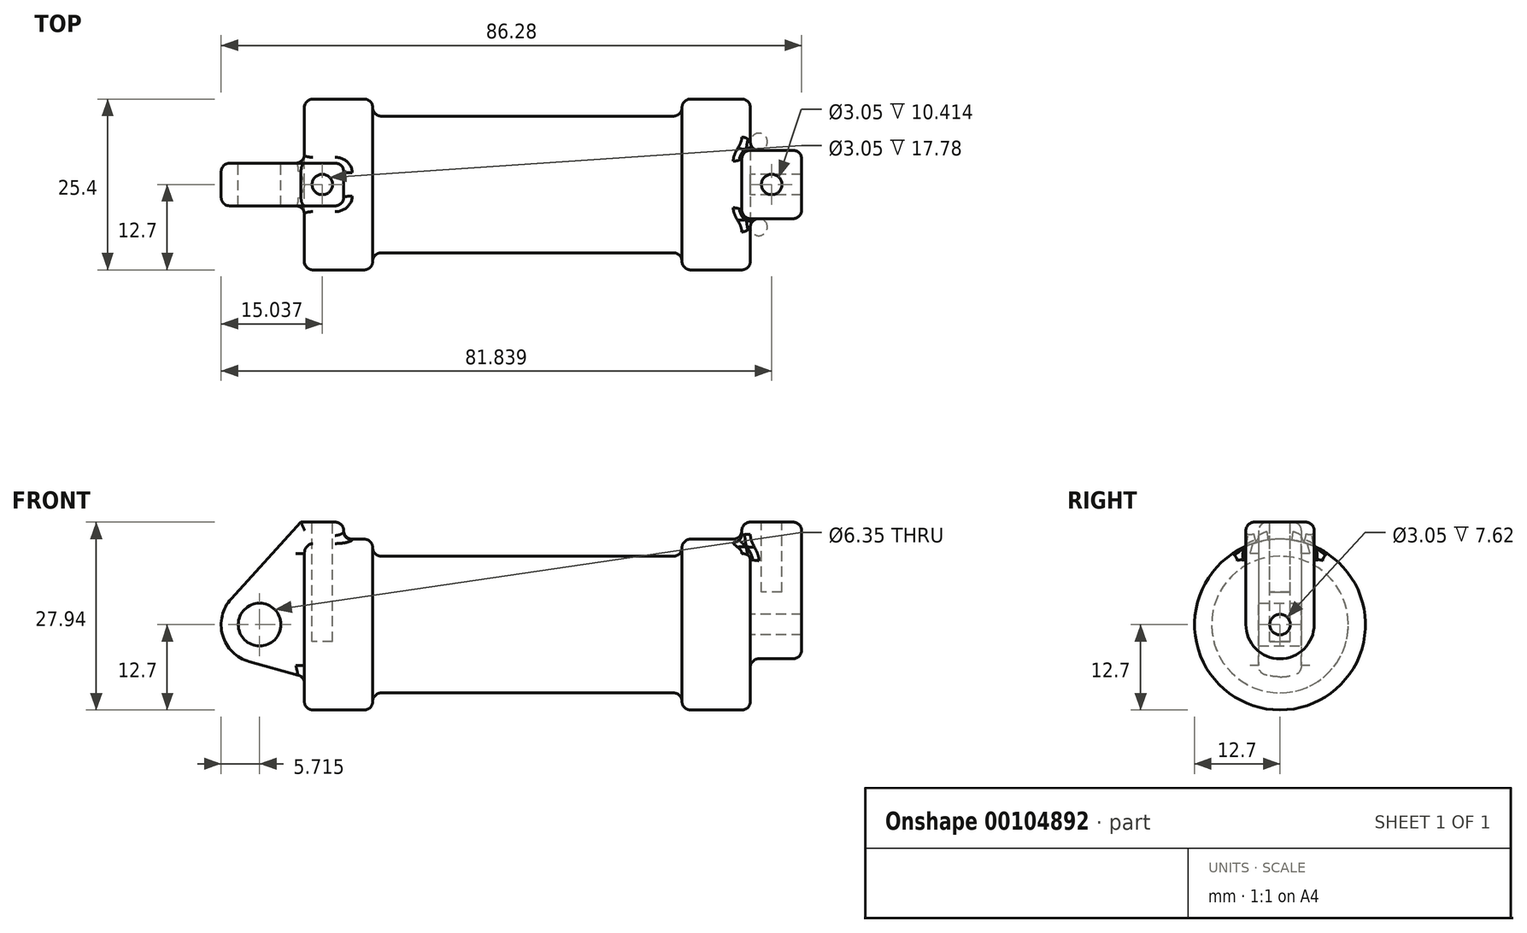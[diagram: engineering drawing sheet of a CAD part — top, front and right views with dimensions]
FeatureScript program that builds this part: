
annotation { "Feature Type Name" : "Feature", "Feature Type Description" : "" }
export const myFeature = defineFeature(function(context is Context, id is Id, definition is map)
    precondition{}
    {
        {
            var Q0;
            Q0=qCreatedBy(makeId("Front.planeOp"),FACE);
            var sketch = newSketch(context, id + "F0", { "sketchPlane" : qUnion([Q0])});
            skLineSegment(sketch, "E0", {"start": v(0, 0) * mm, "end": v(0, 12.7) * mm});
            skLineSegment(sketch, "E1", {"start": v(0, 12.7) * mm, "end": v(10.16, 12.7) * mm});
            skLineSegment(sketch, "E2", {"start": v(10.16, 12.7) * mm, "end": v(10.16, 10.16) * mm});
            skLineSegment(sketch, "E3", {"start": v(10.16, 10.16) * mm, "end": v(56.13, 10.16) * mm});
            skLineSegment(sketch, "E4", {"start": v(56.13, 10.16) * mm, "end": v(56.13, 12.7) * mm});
            skLineSegment(sketch, "E5", {"start": v(56.13, 12.7) * mm, "end": v(66.3, 12.7) * mm});
            skLineSegment(sketch, "E6", {"start": v(66.3, 12.7) * mm, "end": v(66.3, 0) * mm});
            skLineSegment(sketch, "E7", {"start": v(66.3, 0) * mm, "end": v(0, 0) * mm});
            skLineSegment(sketch, "E8", {"start": v(5.84, 15.24) * mm, "end": v(-0.5, 15.24) * mm});
            skLineSegment(sketch, "E9", {"start": v(-0.5, 15.24) * mm, "end": v(-10.88, 3.85) * mm});
            skLineSegment(sketch, "E10", {"start": v(0, 0) * mm, "end": v(-6.65, 0) * mm});
            skCircle(sketch, "E11", {"center": v(-6.65, 0) * mm, "radius": 5.72 * mm});
            skCircle(sketch, "E12", {"center": v(-6.65, 0) * mm, "radius": 3.18 * mm});
            skLineSegment(sketch, "E13", {"start": v(5.84, 15.24) * mm, "end": v(5.84, -9.4) * mm});
            skLineSegment(sketch, "E14", {"start": v(5.84, -9.4) * mm, "end": v(-8.18, -5.5) * mm});
            skSolve(sketch);
        }
        {
            var Q0;
            {var subQ0=sQuery(id+"F0.wireOp",EDGE,"E2");Q0=makeQuery(id+"F0.imprint","IMPRINT",FACE,{"disambiguationData":[TD([[makeQuery(id+"F0.imprint","IMPRINT",EDGE,{"derivedFrom":subQ0}),-1.0]])]});}
            var Q1;
            {var subQ0=sQuery(id+"F0.wireOp",EDGE,"E0");Q1=makeQuery(id+"F0.imprint","IMPRINT",FACE,{"disambiguationData":[TD([[makeQuery(id+"F0.imprint","IMPRINT",EDGE,{"derivedFrom":subQ0}),-1.0]])]});}
            var Q2;
            Q2=sQuery(id+"F0.wireOp",EDGE,"E7");
            revolve(context, id + "F1", {"entities" : qUnion([Q0, Q1]), "axis" : qUnion([Q2]), "revolveType" : RevolveType.FULL});
        }
        {
            var Q0;
            {var subQ0=sQuery(id+"F0.wireOp",EDGE,"E0");Q0=makeQuery(id+"F0.imprint","IMPRINT",FACE,{"disambiguationData":[TD([[makeQuery(id+"F0.imprint","IMPRINT",EDGE,{"derivedFrom":subQ0}),-1.0]])]});}
            var Q1;
            {var subQ3=sQuery(id+"F0.wireOp",EDGE,"E0");Q1=makeQuery(id+"F0.imprint","IMPRINT",FACE,{"disambiguationData":[TD([[makeQuery(id+"F0.imprint","IMPRINT",EDGE,{"derivedFrom":subQ3}),1.0]])]});}
            var Q2;
            {var subQ4=sQuery(id+"F0.wireOp",EDGE,"E12");Q2=makeQuery(id+"F0.imprint","IMPRINT",FACE,{"disambiguationData":[TD([[makeQuery(id+"F0.imprint","IMPRINT",EDGE,{"derivedFrom":subQ4}),-1.0]])]});}
            var Q3;
            {var subQ0=sQuery(id+"F0.wireOp",EDGE,"E14");Q3=makeQuery(id+"F0.imprint","IMPRINT",FACE,{"disambiguationData":[TD([[makeQuery(id+"F0.imprint","IMPRINT",EDGE,{"derivedFrom":subQ0}),-1.0]])]});}
            extrude(context, id + "F2", {"entities" : qUnion([Q0, Q1, Q2, Q3]), "operationType" : NewBodyOperationType.ADD, "depth" : 3.17 * mm, "hasSecondDirection" : true, "secondDirectionOppositeDirection" : true, "secondDirectionDepth" : 3.17 * mm});
        }
        {
            var Q0;
            Q0=makeQuery(id+"F1.opRevolve","SWEPT_FACE",FACE,{"disambiguationData":[OSD([sQuery(id+"F0.wireOp",EDGE,"E6")])]});
            cPlane(context, id + "F3", {"entities" : qUnion([Q0]), "cplaneType" : CPlaneType.OFFSET, "offset" : 0 * mm, "width" : 152.4 * mm, "height" : 152.4 * mm});
        }
        {
            var Q0;
            Q0=qCreatedBy(id+"F3.planeOp",FACE);
            var sketch = newSketch(context, id + "F4", { "sketchPlane" : qUnion([Q0])});
            skCircle(sketch, "E15", {"center": v(0, 0) * mm, "radius": 5.08 * mm});
            skCircle(sketch, "E16", {"center": v(0, 0) * mm, "radius": 1.52 * mm});
            skLineSegment(sketch, "E17", {"start": v(-5.08, 15.24) * mm, "end": v(5.08, 15.24) * mm});
            skLineSegment(sketch, "E18", {"start": v(5.08, 15.24) * mm, "end": v(5.08, 0) * mm});
            skLineSegment(sketch, "E19", {"start": v(-5.08, 15.24) * mm, "end": v(-5.08, 0) * mm});
            skSolve(sketch);
        }
        {
            var Q0;
            Q0 = qSketchRegion(id + "F4", true);
            extrude(context, id + "F5", {"entities" : qUnion([Q0]), "operationType" : NewBodyOperationType.ADD, "depth" : 7.62 * mm, "hasSecondDirection" : true, "secondDirectionOppositeDirection" : true, "secondDirectionDepth" : 1.27 * mm});
        }
        {
            var Q0;
            Q0=makeQuery(id+"F5.opExtrude","SWEPT_FACE",FACE,{"disambiguationData":[OSD([sQuery(id+"F4.wireOp",EDGE,"E17")])]});
            cPlane(context, id + "F6", {"entities" : qUnion([Q0]), "cplaneType" : CPlaneType.OFFSET, "offset" : 0 * mm, "width" : 152.4 * mm, "height" : 152.4 * mm});
        }
        {
            var Q0;
            Q0=qCreatedBy(id+"F6.planeOp",FACE);
            var sketch = newSketch(context, id + "F7", { "sketchPlane" : qUnion([Q0])});
            skCircle(sketch, "E20", {"center": v(69.47, 0) * mm, "radius": 1.52 * mm});
            skLineSegment(sketch, "E21", {"start": v(73.91, 0) * mm, "end": v(65.02, 0) * mm, "construction": true});
            skSolve(sketch);
        }
        {
            var Q0;
            Q0=makeQuery(id+"F7.imprint","IMPRINT",FACE,{"disambiguationData":[TD([[makeQuery(id+"F7.imprint","IMPRINT",EDGE,{"derivedFrom":sQuery(id+"F7.wireOp",EDGE,"E20")}),1.0]])]});
            extrude(context, id + "F8", {"entities" : qUnion([Q0]), "operationType" : NewBodyOperationType.REMOVE, "oppositeDirection" : true, "depth" : 10.4 * mm});
        }
        {
            var Q0;
            Q0=qCreatedBy(id+"F6.planeOp",FACE);
            var sketch = newSketch(context, id + "F9", { "sketchPlane" : qUnion([Q0])});
            skCircle(sketch, "E22", {"center": v(2.67, 0) * mm, "radius": 1.52 * mm});
            skSolve(sketch);
        }
        {
            var Q0;
            Q0 = qSketchRegion(id + "F9", true);
            extrude(context, id + "F10", {"entities" : qUnion([Q0]), "operationType" : NewBodyOperationType.REMOVE, "oppositeDirection" : true, "depth" : 17.78 * mm});
        }
        {
            var Q0;
            Q0=makeQuery(id+"F1.opRevolve","SWEPT_EDGE",EDGE,{"disambiguationData":[OSD([sQuery(id+"F0.wireOp",EDGE,"E1"),sQuery(id+"F0.wireOp",EDGE,"E2")])]});
            var Q1;
            Q1=makeQuery(id+"F1.opRevolve","SWEPT_EDGE",EDGE,{"disambiguationData":[OSD([sQuery(id+"F0.wireOp",EDGE,"E2"),sQuery(id+"F0.wireOp",EDGE,"E3")])]});
            var Q2;
            Q2=makeQuery(id+"F2.boolean.opBoolean","INTERSECT",EDGE,{"derivedFrom":[makeQuery(id+"F1.opRevolve","SWEPT_FACE",FACE,{"disambiguationData":[OSD([sQuery(id+"F0.wireOp",EDGE,"E1")])]}),makeQuery(id+"F2.opExtrude","CAP_FACE",FACE,{"disambiguationData":[OSD([sQuery(id+"F0.wireOp",EDGE,"E8"),sQuery(id+"F0.wireOp",EDGE,"E9"),sQuery(id+"F0.wireOp",EDGE,"E11"),sQuery(id+"F0.wireOp",EDGE,"E12"),sQuery(id+"F0.wireOp",EDGE,"E13"),sQuery(id+"F0.wireOp",EDGE,"E14")])],"isStart":false})]});
            var Q3;
            Q3=makeQuery(id+"F2.boolean.opBoolean","INTERSECT",EDGE,{"derivedFrom":[makeQuery(id+"F1.opRevolve","SWEPT_FACE",FACE,{"disambiguationData":[OSD([sQuery(id+"F0.wireOp",EDGE,"E1")])]}),makeQuery(id+"F2.opExtrude","SWEPT_FACE",FACE,{"disambiguationData":[OSD([sQuery(id+"F0.wireOp",EDGE,"E13")])]})]});
            var Q4;
            Q4=makeQuery(id+"F2.opExtrude","SWEPT_EDGE",EDGE,{"disambiguationData":[OSD([sQuery(id+"F0.wireOp",EDGE,"E8"),sQuery(id+"F0.wireOp",EDGE,"E13")])]});
            var Q5;
            Q5=makeQuery(id+"F2.opExtrude","CAP_EDGE",EDGE,{"disambiguationData":[OSD([sQuery(id+"F0.wireOp",EDGE,"E8")])],"isStart":false});
            var Q6;
            Q6=makeQuery(id+"F2.opExtrude","CAP_EDGE",EDGE,{"disambiguationData":[OSD([sQuery(id+"F0.wireOp",EDGE,"E8")])],"isStart":true});
            var Q7;
            Q7=makeQuery(id+"F2.boolean.opBoolean","INTERSECT",EDGE,{"derivedFrom":[makeQuery(id+"F1.opRevolve","SWEPT_FACE",FACE,{"disambiguationData":[OSD([sQuery(id+"F0.wireOp",EDGE,"E1")])]}),makeQuery(id+"F2.opExtrude","CAP_FACE",FACE,{"disambiguationData":[OSD([sQuery(id+"F0.wireOp",EDGE,"E8"),sQuery(id+"F0.wireOp",EDGE,"E9"),sQuery(id+"F0.wireOp",EDGE,"E11"),sQuery(id+"F0.wireOp",EDGE,"E12"),sQuery(id+"F0.wireOp",EDGE,"E13"),sQuery(id+"F0.wireOp",EDGE,"E14")])],"isStart":true})]});
            var Q8;
            Q8=makeQuery(id+"F2.opExtrude","CAP_EDGE",EDGE,{"disambiguationData":[OSD([sQuery(id+"F0.wireOp",EDGE,"E9")])],"isStart":false});
            var Q9;
            Q9=makeQuery(id+"F2.opExtrude","CAP_EDGE",EDGE,{"disambiguationData":[OSD([sQuery(id+"F0.wireOp",EDGE,"E11")])],"isStart":true});
            var Q10;
            Q10=makeQuery(id+"F2.opExtrude","CAP_EDGE",EDGE,{"disambiguationData":[OSD([sQuery(id+"F0.wireOp",EDGE,"E9")])],"isStart":true});
            var Q11;
            Q11=makeQuery(id+"F2.opExtrude","CAP_EDGE",EDGE,{"disambiguationData":[OSD([sQuery(id+"F0.wireOp",EDGE,"E11")])],"isStart":false});
            var Q12;
            Q12=makeQuery(id+"F2.opExtrude","CAP_EDGE",EDGE,{"disambiguationData":[OSD([sQuery(id+"F0.wireOp",EDGE,"E14")])],"isStart":true});
            var Q13;
            Q13=makeQuery(id+"F2.opExtrude","CAP_EDGE",EDGE,{"disambiguationData":[OSD([sQuery(id+"F0.wireOp",EDGE,"E14")])],"isStart":false});
            var Q14;
            Q14=makeQuery(id+"F2.boolean.opBoolean","INTERSECT",EDGE,{"derivedFrom":[makeQuery(id+"F1.opRevolve","SWEPT_FACE",FACE,{"disambiguationData":[OSD([sQuery(id+"F0.wireOp",EDGE,"E0")])]}),makeQuery(id+"F2.opExtrude","CAP_FACE",FACE,{"disambiguationData":[OSD([sQuery(id+"F0.wireOp",EDGE,"E8"),sQuery(id+"F0.wireOp",EDGE,"E9"),sQuery(id+"F0.wireOp",EDGE,"E11"),sQuery(id+"F0.wireOp",EDGE,"E12"),sQuery(id+"F0.wireOp",EDGE,"E13"),sQuery(id+"F0.wireOp",EDGE,"E14")])],"isStart":false})]});
            var Q15;
            Q15=makeQuery(id+"F2.boolean.opBoolean","INTERSECT",EDGE,{"derivedFrom":[makeQuery(id+"F1.opRevolve","SWEPT_FACE",FACE,{"disambiguationData":[OSD([sQuery(id+"F0.wireOp",EDGE,"E0")])]}),makeQuery(id+"F2.opExtrude","CAP_FACE",FACE,{"disambiguationData":[OSD([sQuery(id+"F0.wireOp",EDGE,"E8"),sQuery(id+"F0.wireOp",EDGE,"E9"),sQuery(id+"F0.wireOp",EDGE,"E11"),sQuery(id+"F0.wireOp",EDGE,"E12"),sQuery(id+"F0.wireOp",EDGE,"E13"),sQuery(id+"F0.wireOp",EDGE,"E14")])],"isStart":true})]});
            var Q16;
            Q16=makeQuery(id+"F5.opExtrude","CAP_EDGE",EDGE,{"disambiguationData":[OSD([sQuery(id+"F4.wireOp",EDGE,"E17")])],"isStart":false});
            var Q17;
            Q17=makeQuery(id+"F5.opExtrude","SWEPT_EDGE",EDGE,{"disambiguationData":[OSD([sQuery(id+"F4.wireOp",EDGE,"E17"),sQuery(id+"F4.wireOp",EDGE,"E18")])]});
            var Q18;
            Q18=makeQuery(id+"F5.opExtrude","CAP_EDGE",EDGE,{"disambiguationData":[OSD([sQuery(id+"F4.wireOp",EDGE,"E18")])],"isStart":false});
            var Q19;
            Q19=makeQuery(id+"F5.boolean.opBoolean","INTERSECT",EDGE,{"derivedFrom":[makeQuery(id+"F1.opRevolve","SWEPT_FACE",FACE,{"disambiguationData":[OSD([sQuery(id+"F0.wireOp",EDGE,"E6")])]}),makeQuery(id+"F5.opExtrude","SWEPT_FACE",FACE,{"disambiguationData":[OSD([sQuery(id+"F4.wireOp",EDGE,"E18")])]})]});
            var Q20;
            Q20=makeQuery(id+"F5.boolean.opBoolean","INTERSECT",EDGE,{"derivedFrom":[makeQuery(id+"F1.opRevolve","SWEPT_FACE",FACE,{"disambiguationData":[OSD([sQuery(id+"F0.wireOp",EDGE,"E5")])]}),makeQuery(id+"F5.opExtrude","SWEPT_FACE",FACE,{"disambiguationData":[OSD([sQuery(id+"F4.wireOp",EDGE,"E18")])]})]});
            var Q21;
            Q21=makeQuery(id+"F5.opExtrude","SWEPT_EDGE",EDGE,{"disambiguationData":[OSD([sQuery(id+"F4.wireOp",EDGE,"E15"),sQuery(id+"F4.wireOp",EDGE,"E18")])]});
            var Q22;
            Q22=makeQuery(id+"F5.boolean.opBoolean","INTERSECT",EDGE,{"derivedFrom":[makeQuery(id+"F1.opRevolve","SWEPT_FACE",FACE,{"disambiguationData":[OSD([sQuery(id+"F0.wireOp",EDGE,"E6")])]}),makeQuery(id+"F5.opExtrude","SWEPT_FACE",FACE,{"disambiguationData":[OSD([sQuery(id+"F4.wireOp",EDGE,"E15")])]})]});
            var Q23;
            Q23=makeQuery(id+"F5.opExtrude","SWEPT_EDGE",EDGE,{"disambiguationData":[OSD([sQuery(id+"F4.wireOp",EDGE,"E17"),sQuery(id+"F4.wireOp",EDGE,"E19")])]});
            var Q24;
            Q24=makeQuery(id+"F5.opExtrude","CAP_EDGE",EDGE,{"disambiguationData":[OSD([sQuery(id+"F4.wireOp",EDGE,"E19")])],"isStart":false});
            var Q25;
            Q25=makeQuery(id+"F5.boolean.opBoolean","INTERSECT",EDGE,{"derivedFrom":[makeQuery(id+"F1.opRevolve","SWEPT_FACE",FACE,{"disambiguationData":[OSD([sQuery(id+"F0.wireOp",EDGE,"E6")])]}),makeQuery(id+"F5.opExtrude","SWEPT_FACE",FACE,{"disambiguationData":[OSD([sQuery(id+"F4.wireOp",EDGE,"E19")])]})]});
            var Q26;
            Q26=makeQuery(id+"F5.boolean.opBoolean","INTERSECT",EDGE,{"derivedFrom":[makeQuery(id+"F1.opRevolve","SWEPT_FACE",FACE,{"disambiguationData":[OSD([sQuery(id+"F0.wireOp",EDGE,"E5")])]}),makeQuery(id+"F5.opExtrude","SWEPT_FACE",FACE,{"disambiguationData":[OSD([sQuery(id+"F4.wireOp",EDGE,"E19")])]})]});
            var Q27;
            Q27=makeQuery(id+"F1.opRevolve","SWEPT_EDGE",EDGE,{"disambiguationData":[OSD([sQuery(id+"F0.wireOp",EDGE,"E5"),sQuery(id+"F0.wireOp",EDGE,"E6")])]});
            var Q28;
            Q28=makeQuery(id+"F5.opExtrude","CAP_EDGE",EDGE,{"disambiguationData":[OSD([sQuery(id+"F4.wireOp",EDGE,"E15")])],"isStart":false});
            var Q29;
            Q29=makeQuery(id+"F1.opRevolve","SWEPT_EDGE",EDGE,{"disambiguationData":[OSD([sQuery(id+"F0.wireOp",EDGE,"E3"),sQuery(id+"F0.wireOp",EDGE,"E4")])]});
            var Q30;
            Q30=makeQuery(id+"F1.opRevolve","SWEPT_EDGE",EDGE,{"disambiguationData":[OSD([sQuery(id+"F0.wireOp",EDGE,"E4"),sQuery(id+"F0.wireOp",EDGE,"E5")])]});
            var Q31;
            Q31=makeQuery(id+"F5.opExtrude","CAP_EDGE",EDGE,{"disambiguationData":[OSD([sQuery(id+"F4.wireOp",EDGE,"E17")])],"isStart":true});
            var Q32;
            Q32=makeQuery(id+"F5.opExtrude","CAP_EDGE",EDGE,{"disambiguationData":[OSD([sQuery(id+"F4.wireOp",EDGE,"E18")])],"isStart":true});
            var Q33;
            Q33=makeQuery(id+"F5.boolean.opBoolean","INTERSECT",EDGE,{"derivedFrom":[makeQuery(id+"F1.opRevolve","SWEPT_FACE",FACE,{"disambiguationData":[OSD([sQuery(id+"F0.wireOp",EDGE,"E5")])]}),makeQuery(id+"F5.opExtrude","CAP_FACE",FACE,{"disambiguationData":[OSD([sQuery(id+"F4.wireOp",EDGE,"E15"),sQuery(id+"F4.wireOp",EDGE,"E16"),sQuery(id+"F4.wireOp",EDGE,"E17"),sQuery(id+"F4.wireOp",EDGE,"E18"),sQuery(id+"F4.wireOp",EDGE,"E19")])],"isStart":true})]});
            var Q34;
            Q34=makeQuery(id+"F5.opExtrude","CAP_EDGE",EDGE,{"disambiguationData":[OSD([sQuery(id+"F4.wireOp",EDGE,"E19")])],"isStart":true});
            var Q35;
            Q35=makeQuery(id+"F2.opExtrude","CAP_EDGE",EDGE,{"disambiguationData":[OSD([sQuery(id+"F0.wireOp",EDGE,"E13")])],"isStart":false});
            var Q36;
            Q36=makeQuery(id+"F2.opExtrude","CAP_EDGE",EDGE,{"disambiguationData":[OSD([sQuery(id+"F0.wireOp",EDGE,"E13")])],"isStart":true});
            var Q37;
            Q37=makeQuery(id+"F1.opRevolve","SWEPT_EDGE",EDGE,{"disambiguationData":[OSD([sQuery(id+"F0.wireOp",EDGE,"E0"),sQuery(id+"F0.wireOp",EDGE,"E1")])]});
            fillet(context, id + "F11", {"entities" : qUnion([Q0, Q1, Q2, Q3, Q4, Q5, Q6, Q7, Q8, Q9, Q10, Q11, Q12, Q13, Q14, Q15, Q16, Q17, Q18, Q19, Q20, Q21, Q22, Q23, Q24, Q25, Q26, Q27, Q28, Q29, Q30, Q31, Q32, Q33, Q34, Q35, Q36, Q37]), "radius" : 1.27 * mm, "tangentPropagation" : true, "allowEdgeOverflow" : false});
        }
    });
